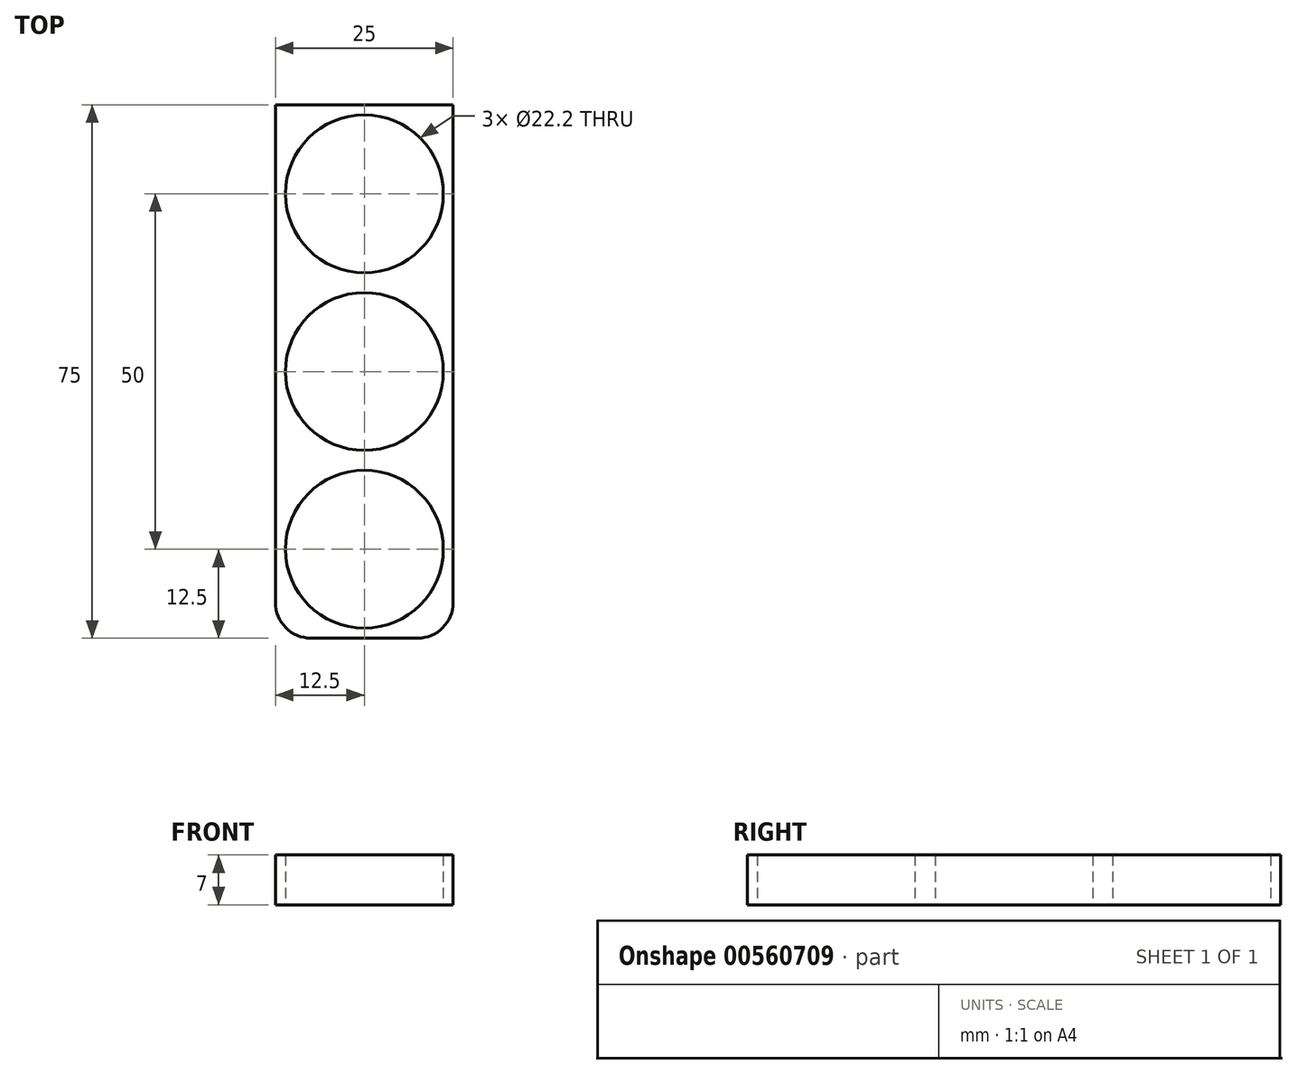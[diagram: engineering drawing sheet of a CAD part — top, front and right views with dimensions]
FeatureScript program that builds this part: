
annotation { "Feature Type Name" : "Feature", "Feature Type Description" : "" }
export const myFeature = defineFeature(function(context is Context, id is Id, definition is map)
    precondition{}
    {
        {
            var Q0;
            Q0=qCreatedBy(makeId("Top.planeOp"),FACE);
            var sketch = newSketch(context, id + "F0", { "sketchPlane" : qUnion([Q0])});
            skCircle(sketch, "E0", {"center": v(0, 0) * mm, "radius": 11.1 * mm});
            skLineSegment(sketch, "E1.bottom", {"start": v(12.5, 37.5) * mm, "end": v(-12.5, 37.5) * mm});
            skLineSegment(sketch, "E1.top", {"start": v(12.5, -37.5) * mm, "end": v(-12.5, -37.5) * mm});
            skLineSegment(sketch, "E1.left", {"start": v(12.5, 37.5) * mm, "end": v(12.5, -37.5) * mm});
            skLineSegment(sketch, "E1.right", {"start": v(-12.5, 37.5) * mm, "end": v(-12.5, -37.5) * mm});
            skLineSegment(sketch, "E2.bottom", {"start": v(-12.5, 37.5) * mm, "end": v(12.5, 37.5) * mm});
            skLineSegment(sketch, "E2.left", {"start": v(-12.5, 37.5) * mm, "end": v(-12.5, 12.5) * mm});
            skLineSegment(sketch, "E2.right", {"start": v(12.5, 37.5) * mm, "end": v(12.5, 12.5) * mm});
            skLineSegment(sketch, "E3.left", {"start": v(-12.5, 12.5) * mm, "end": v(-12.5, -12.5) * mm});
            skLineSegment(sketch, "E3.right", {"start": v(12.5, 12.5) * mm, "end": v(12.5, -12.5) * mm});
            skLineSegment(sketch, "E4.left", {"start": v(-12.5, 37.5) * mm, "end": v(-12.5, 25) * mm});
            skLineSegment(sketch, "E4.right", {"start": v(12.5, 37.5) * mm, "end": v(12.5, 25) * mm});
            skLineSegment(sketch, "E5.left", {"start": v(-12.5, -12.5) * mm, "end": v(-12.5, -25) * mm});
            skLineSegment(sketch, "E5.right", {"start": v(12.5, -12.5) * mm, "end": v(12.5, -25) * mm});
            skCircle(sketch, "E6", {"center": v(0, 25) * mm, "radius": 11.1 * mm});
            skCircle(sketch, "E7", {"center": v(0, -25) * mm, "radius": 11.1 * mm});
            skSolve(sketch);
        }
        {
            var Q0;
            Q0=makeQuery(id+"F0.imprint","IMPRINT",FACE,{"disambiguationData":[TD([[makeQuery(id+"F0.imprint","IMPRINT",EDGE,{"derivedFrom":sQuery(id+"F0.wireOp",EDGE,"E0")}),-1.0]])]});
            extrude(context, id + "F1", {"entities" : qUnion([Q0]), "depth" : 7 * mm, "offsetDistance" : 25 * mm});
        }
        {
            var Q0;
            Q0=makeQuery(id+"F1.opExtrude","SWEPT_EDGE",EDGE,{"disambiguationData":[OSD([sQuery(id+"F0.wireOp",EDGE,"E1.top"),sQuery(id+"F0.wireOp",EDGE,"E1.left")])]});
            var Q1;
            Q1=makeQuery(id+"F1.opExtrude","SWEPT_EDGE",EDGE,{"disambiguationData":[OSD([sQuery(id+"F0.wireOp",EDGE,"E1.top"),sQuery(id+"F0.wireOp",EDGE,"E1.right")])]});
            var Q2;
            Q2=makeQuery(id+"F1.opExtrude","SWEPT_EDGE",EDGE,{"disambiguationData":[OSD([sQuery(id+"F0.wireOp",EDGE,"E2.bottom"),sQuery(id+"F0.wireOp",EDGE,"E4.left")])]});
            var Q3;
            Q3=makeQuery(id+"F1.opExtrude","SWEPT_EDGE",EDGE,{"disambiguationData":[OSD([sQuery(id+"F0.wireOp",EDGE,"E2.bottom"),sQuery(id+"F0.wireOp",EDGE,"E4.right")])]});
            fillet(context, id + "F2", {"entities" : qUnion([Q0, Q1, Q2, Q3]), "radius" : 5 * mm, "tangentPropagation" : true, "allowEdgeOverflow" : false});
        }
    });
